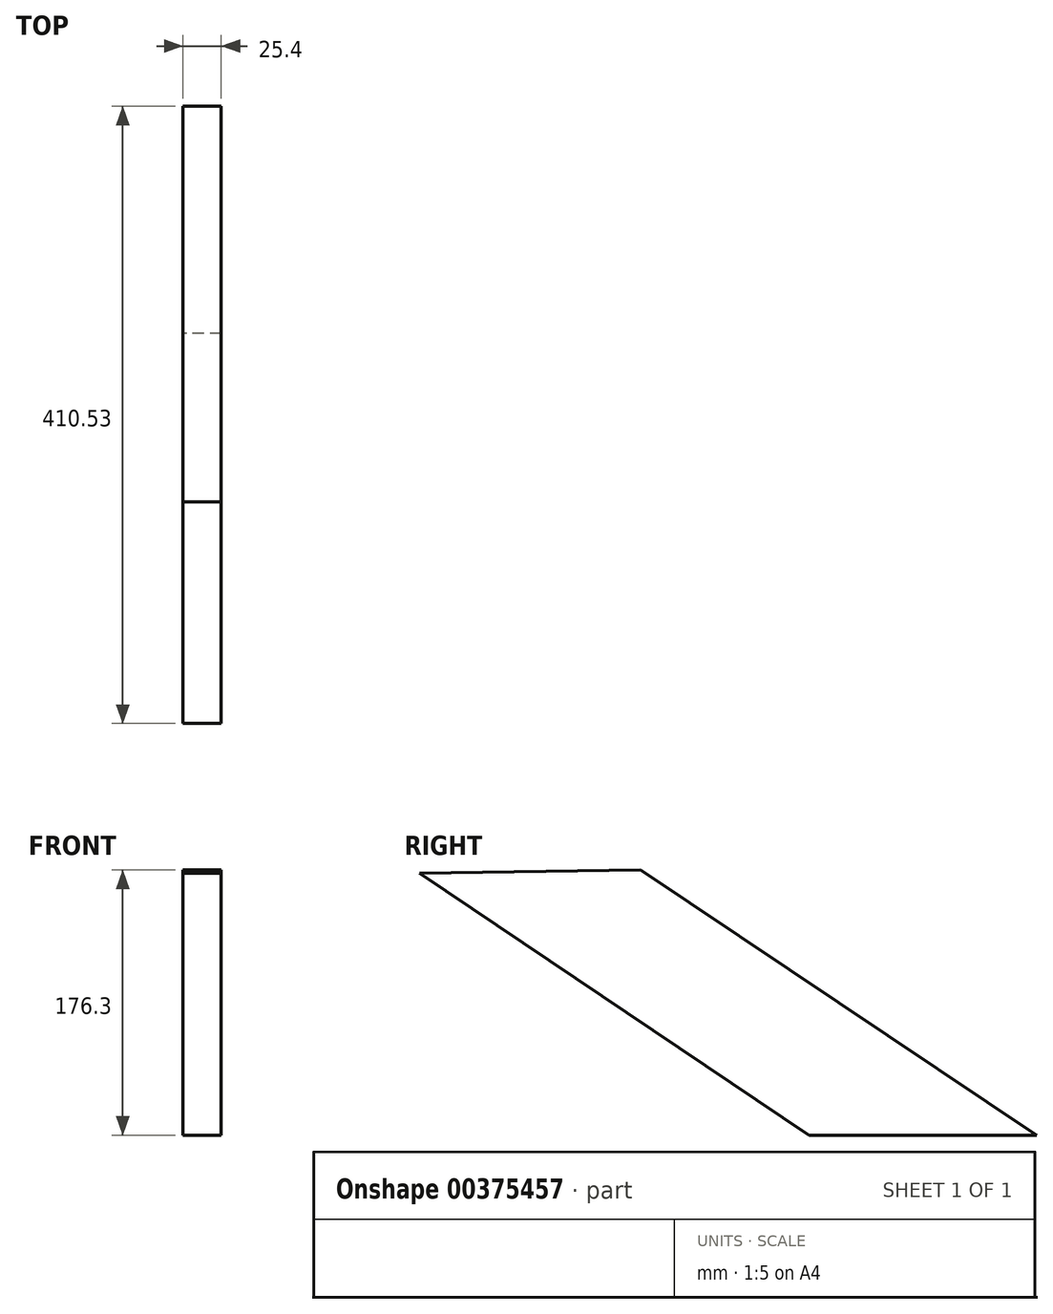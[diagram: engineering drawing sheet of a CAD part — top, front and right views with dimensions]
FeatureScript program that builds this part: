
annotation { "Feature Type Name" : "Feature", "Feature Type Description" : "" }
export const myFeature = defineFeature(function(context is Context, id is Id, definition is map)
    precondition{}
    {
        {
            var Q0;
            Q0=qCreatedBy(makeId("Right.planeOp"),FACE);
            var sketch = newSketch(context, id + "F0", { "sketchPlane" : qUnion([Q0])});
            skLineSegment(sketch, "E0", {"start": v(0, 0) * mm, "end": v(-203.43, 86.1) * mm});
            skLineSegment(sketch, "E1", {"start": v(0, 0) * mm, "end": v(207.1, -87.94) * mm});
            skLineSegment(sketch, "E2", {"start": v(0, 0) * mm, "end": v(55.9, -87.94) * mm});
            skLineSegment(sketch, "E3", {"start": v(0, 0) * mm, "end": v(-56.16, 88.36) * mm});
            skLineSegment(sketch, "E4", {"start": v(-203.43, 86.1) * mm, "end": v(55.9, -87.94) * mm});
            skLineSegment(sketch, "E5", {"start": v(-203.43, 86.1) * mm, "end": v(-56.16, 88.36) * mm});
            skLineSegment(sketch, "E6", {"start": v(-56.16, 88.36) * mm, "end": v(207.1, -87.94) * mm});
            skLineSegment(sketch, "E7", {"start": v(207.1, -87.94) * mm, "end": v(55.9, -87.94) * mm});
            skSolve(sketch);
        }
        {
            var Q0;
            Q0 = qSketchRegion(id + "F0", true);
            extrude(context, id + "F1", {"entities" : qUnion([Q0]), "depth" : 25.4 * mm});
        }
    });
